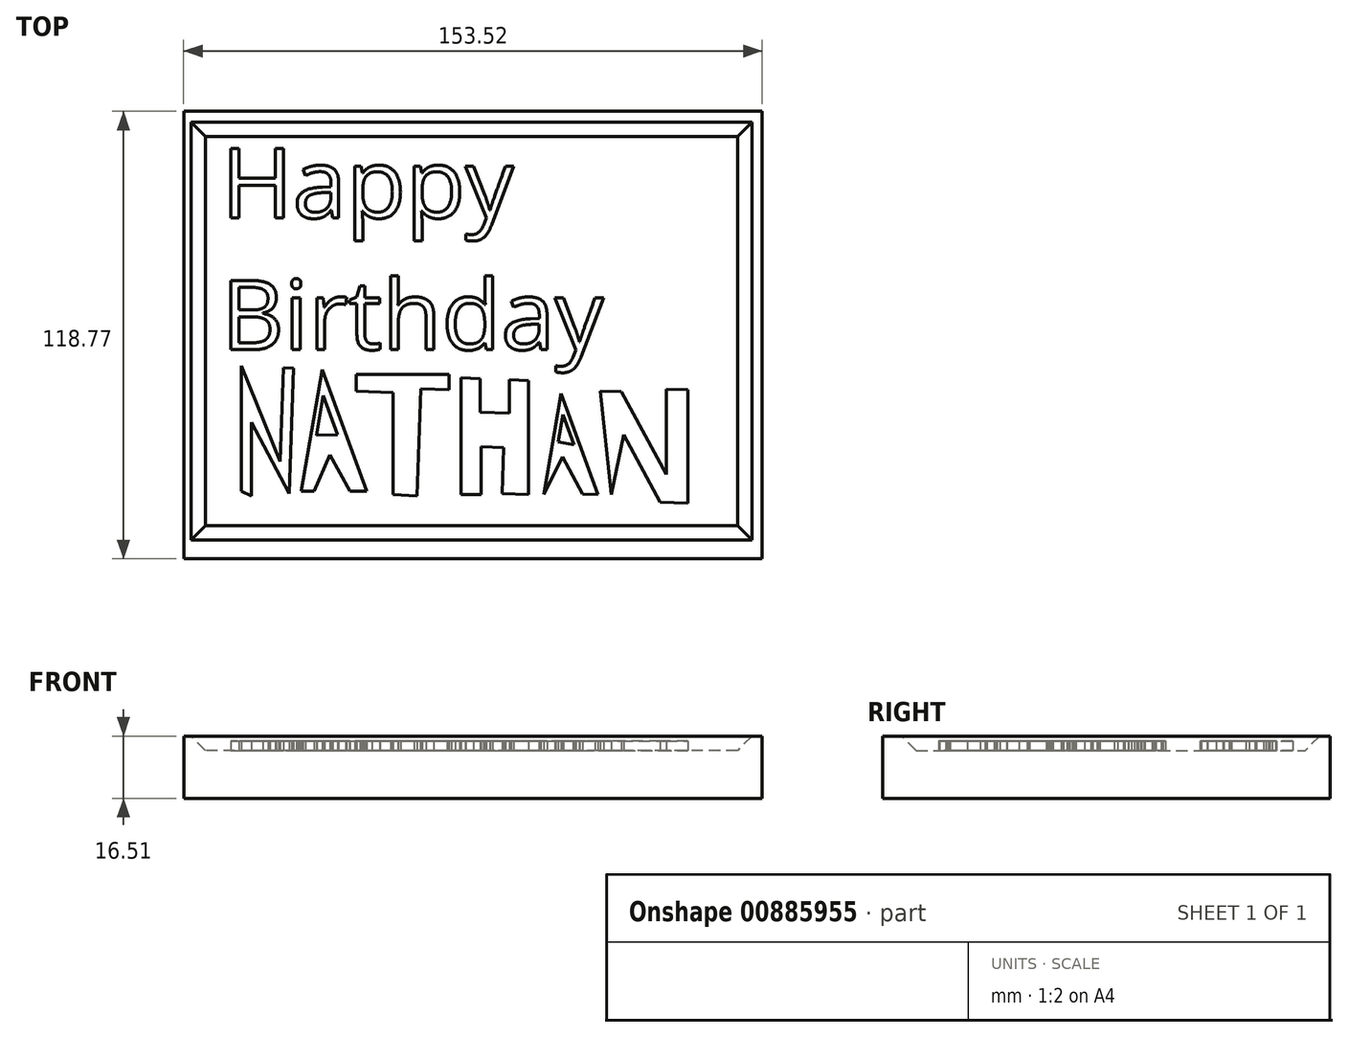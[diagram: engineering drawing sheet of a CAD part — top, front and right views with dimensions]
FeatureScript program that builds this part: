
annotation { "Feature Type Name" : "Feature", "Feature Type Description" : "" }
export const myFeature = defineFeature(function(context is Context, id is Id, definition is map)
    precondition{}
    {
        {
            var Q0;
            Q0=qCreatedBy(makeId("Top.planeOp"),FACE);
            var sketch = newSketch(context, id + "F0", { "sketchPlane" : qUnion([Q0])});
            skText(sketch, "E0", { "text": "Happy\nBirthday", "fontName": "OpenSans-Regular.ttf"});
            skLineSegment(sketch, "E1", {"start": v(-85.3, -54.38) * mm, "end": v(-85.3, -21.05) * mm});
            skLineSegment(sketch, "E2", {"start": v(-85.3, -21.05) * mm, "end": v(-74.93, -46.48) * mm});
            skLineSegment(sketch, "E3", {"start": v(-74.93, -46.48) * mm, "end": v(-74.07, -21.54) * mm});
            skLineSegment(sketch, "E4", {"start": v(-74.07, -21.54) * mm, "end": v(-71.34, -21.64) * mm});
            skLineSegment(sketch, "E5", {"start": v(-71.34, -21.64) * mm, "end": v(-72.5, -55) * mm});
            skLineSegment(sketch, "E6", {"start": v(-72.5, -55) * mm, "end": v(-82.59, -36.1) * mm});
            skLineSegment(sketch, "E7", {"start": v(-82.59, -36.1) * mm, "end": v(-82.59, -55.61) * mm});
            skLineSegment(sketch, "E8", {"start": v(-82.59, -55.61) * mm, "end": v(-85.3, -54.38) * mm});
            skLineSegment(sketch, "E9", {"start": v(-69.38, -54.38) * mm, "end": v(-63.82, -22.03) * mm});
            skLineSegment(sketch, "E10", {"start": v(-63.82, -22.03) * mm, "end": v(-51.97, -54.38) * mm});
            skLineSegment(sketch, "E11", {"start": v(-51.97, -54.38) * mm, "end": v(-56.42, -54.38) * mm});
            skLineSegment(sketch, "E12", {"start": v(-65.35, -39.43) * mm, "end": v(-63.54, -28.9) * mm});
            skLineSegment(sketch, "E13", {"start": v(-63.54, -28.9) * mm, "end": v(-59.72, -39.31) * mm});
            skLineSegment(sketch, "E14", {"start": v(-56.42, -54.38) * mm, "end": v(-61.7, -44.62) * mm});
            skLineSegment(sketch, "E15", {"start": v(-61.7, -44.62) * mm, "end": v(-65.95, -54.38) * mm});
            skLineSegment(sketch, "E16", {"start": v(-65.95, -54.38) * mm, "end": v(-69.38, -54.38) * mm});
            skLineSegment(sketch, "E17", {"start": v(-65.35, -39.43) * mm, "end": v(-59.72, -39.31) * mm});
            skLineSegment(sketch, "E18", {"start": v(-44.97, -55.18) * mm, "end": v(-44.97, -28.11) * mm});
            skLineSegment(sketch, "E19", {"start": v(-44.97, -28.11) * mm, "end": v(-54.75, -27.78) * mm});
            skLineSegment(sketch, "E20", {"start": v(-54.75, -27.78) * mm, "end": v(-54.75, -23.4) * mm});
            skLineSegment(sketch, "E21", {"start": v(-54.75, -23.4) * mm, "end": v(-30.13, -23.4) * mm});
            skLineSegment(sketch, "E22", {"start": v(-30.13, -23.4) * mm, "end": v(-30.13, -27.42) * mm});
            skLineSegment(sketch, "E23", {"start": v(-30.13, -27.42) * mm, "end": v(-37.62, -27.16) * mm});
            skLineSegment(sketch, "E24", {"start": v(-37.62, -27.16) * mm, "end": v(-38.6, -55.57) * mm});
            skLineSegment(sketch, "E25", {"start": v(-38.6, -55.57) * mm, "end": v(-44.97, -55.18) * mm});
            skLineSegment(sketch, "E26", {"start": v(-26.99, -55.18) * mm, "end": v(-26.99, -24.27) * mm});
            skLineSegment(sketch, "E27", {"start": v(-26.99, -24.27) * mm, "end": v(-21.92, -24.45) * mm});
            skLineSegment(sketch, "E28", {"start": v(-21.92, -24.45) * mm, "end": v(-21.92, -33.35) * mm});
            skLineSegment(sketch, "E29", {"start": v(-21.92, -33.35) * mm, "end": v(-14.07, -33.62) * mm});
            skLineSegment(sketch, "E30", {"start": v(-14.07, -33.62) * mm, "end": v(-14.07, -24.8) * mm});
            skLineSegment(sketch, "E31", {"start": v(-14.07, -24.8) * mm, "end": v(-9.01, -24.97) * mm});
            skLineSegment(sketch, "E32", {"start": v(-9.01, -24.97) * mm, "end": v(-9.01, -55.18) * mm});
            skLineSegment(sketch, "E33", {"start": v(-9.01, -55.18) * mm, "end": v(-16.02, -54.93) * mm});
            skLineSegment(sketch, "E34", {"start": v(-16.02, -54.93) * mm, "end": v(-15.6, -42.75) * mm});
            skLineSegment(sketch, "E35", {"start": v(-15.6, -42.75) * mm, "end": v(-21.57, -42.54) * mm});
            skLineSegment(sketch, "E36", {"start": v(-21.57, -42.54) * mm, "end": v(-21.57, -55.18) * mm});
            skLineSegment(sketch, "E37", {"start": v(-21.57, -55.18) * mm, "end": v(-26.99, -55.18) * mm});
            skLineSegment(sketch, "E38", {"start": v(-5, -55.18) * mm, "end": v(-0.4, -28.38) * mm});
            skLineSegment(sketch, "E39", {"start": v(-0.4, -28.38) * mm, "end": v(9.42, -55.18) * mm});
            skLineSegment(sketch, "E40", {"start": v(9.42, -55.18) * mm, "end": v(5.36, -55.03) * mm});
            skLineSegment(sketch, "E41", {"start": v(5.36, -55.03) * mm, "end": v(0, -45.13) * mm});
            skLineSegment(sketch, "E42", {"start": v(0, -45.13) * mm, "end": v(-5, -55.18) * mm});
            skLineSegment(sketch, "E43", {"start": v(-1.12, -41.23) * mm, "end": v(0.13, -33.96) * mm});
            skLineSegment(sketch, "E44", {"start": v(0.13, -33.96) * mm, "end": v(3.07, -41.97) * mm});
            skLineSegment(sketch, "E45", {"start": v(3.07, -41.97) * mm, "end": v(-1.12, -41.23) * mm});
            skLineSegment(sketch, "E46", {"start": v(12.92, -55.18) * mm, "end": v(10.01, -27.76) * mm});
            skLineSegment(sketch, "E47", {"start": v(10.01, -27.76) * mm, "end": v(15.6, -27.95) * mm});
            skLineSegment(sketch, "E48", {"start": v(15.6, -27.95) * mm, "end": v(27.48, -49.9) * mm});
            skLineSegment(sketch, "E49", {"start": v(27.48, -49.9) * mm, "end": v(27.48, -27.22) * mm});
            skLineSegment(sketch, "E50", {"start": v(27.48, -27.22) * mm, "end": v(33.28, -27.42) * mm});
            skLineSegment(sketch, "E51", {"start": v(33.28, -27.42) * mm, "end": v(33.28, -57.46) * mm});
            skLineSegment(sketch, "E52", {"start": v(33.28, -57.46) * mm, "end": v(25.91, -57.2) * mm});
            skLineSegment(sketch, "E53", {"start": v(25.91, -57.2) * mm, "end": v(16.23, -39.31) * mm});
            skLineSegment(sketch, "E54", {"start": v(16.23, -39.31) * mm, "end": v(12.92, -55.18) * mm});
            const initialGuessF0  = {"E0": [-0.09058, 0.0182, 1, 0, 0.0185]};
            skSetInitialGuess(sketch, initialGuessF0);
            skSolve(sketch);
        }
        {
            var Q0;
            Q0=qCreatedBy(makeId("Top.planeOp"),FACE);
            var sketch = newSketch(context, id + "F1", { "sketchPlane" : qUnion([Q0])});
            skLineSegment(sketch, "E55.bottom", {"start": v(-93.53, 38.56) * mm, "end": v(45.16, 38.56) * mm});
            skLineSegment(sketch, "E55.top", {"start": v(-93.53, -62.17) * mm, "end": v(45.16, -62.17) * mm});
            skLineSegment(sketch, "E55.left", {"start": v(-93.53, 38.56) * mm, "end": v(-93.53, -62.17) * mm});
            skLineSegment(sketch, "E55.right", {"start": v(45.16, 38.56) * mm, "end": v(45.16, -62.17) * mm});
            skLineSegment(sketch, "E56.bottom", {"start": v(52.97, 46.47) * mm, "end": v(-100.55, 46.47) * mm});
            skLineSegment(sketch, "E56.top", {"start": v(52.97, -72.3) * mm, "end": v(-100.55, -72.3) * mm});
            skLineSegment(sketch, "E56.left", {"start": v(52.97, 46.47) * mm, "end": v(52.97, -72.3) * mm});
            skLineSegment(sketch, "E56.right", {"start": v(-100.55, 46.47) * mm, "end": v(-100.55, -72.3) * mm});
            skSolve(sketch);
        }
        {
            var Q0;
            Q0=makeQuery(id+"F1.imprint","IMPRINT",FACE,{"disambiguationData":[TD([[makeQuery(id+"F1.imprint","IMPRINT",EDGE,{"derivedFrom":sQuery(id+"F1.wireOp",EDGE,"E55.bottom")}),1.0]])]});
            extrude(context, id + "F2", {"entities" : qUnion([Q0]), "depth" : 16.5 * mm, "offsetDistance" : 25.4 * mm});
        }
        {
            var Q0;
            Q0=makeQuery(id+"F1.imprint","IMPRINT",FACE,{"disambiguationData":[TD([[makeQuery(id+"F1.imprint","IMPRINT",EDGE,{"derivedFrom":sQuery(id+"F1.wireOp",EDGE,"E55.bottom")}),-1.0]])]});
            extrude(context, id + "F3", {"entities" : qUnion([Q0]), "operationType" : NewBodyOperationType.ADD, "depth" : 12.7 * mm, "offsetDistance" : 25.4 * mm});
        }
        {
            var Q0;
            Q0 = qSketchRegion(id + "F0", true);
            extrude(context, id + "F4", {"entities" : qUnion([Q0]), "operationType" : NewBodyOperationType.ADD, "depth" : 15.24 * mm, "offsetDistance" : 25.4 * mm});
        }
        {
            var Q0;
            Q0=makeQuery(id+"F2.opExtrude","CAP_EDGE",EDGE,{"disambiguationData":[OSD([sQuery(id+"F1.wireOp",EDGE,"E55.bottom")])],"isStart":false});
            var Q1;
            Q1=makeQuery(id+"F2.opExtrude","CAP_EDGE",EDGE,{"disambiguationData":[OSD([sQuery(id+"F1.wireOp",EDGE,"E55.right")])],"isStart":false});
            var Q2;
            Q2=makeQuery(id+"F2.opExtrude","CAP_EDGE",EDGE,{"disambiguationData":[OSD([sQuery(id+"F1.wireOp",EDGE,"E55.top")])],"isStart":false});
            var Q3;
            Q3=makeQuery(id+"F2.opExtrude","CAP_EDGE",EDGE,{"disambiguationData":[OSD([sQuery(id+"F1.wireOp",EDGE,"E55.left")])],"isStart":false});
            chamfer(context, id + "F5", {"entities" : qUnion([Q0, Q1, Q2, Q3]), "width" : 5.08 * mm, "tangentPropagation" : true});
        }
    });
